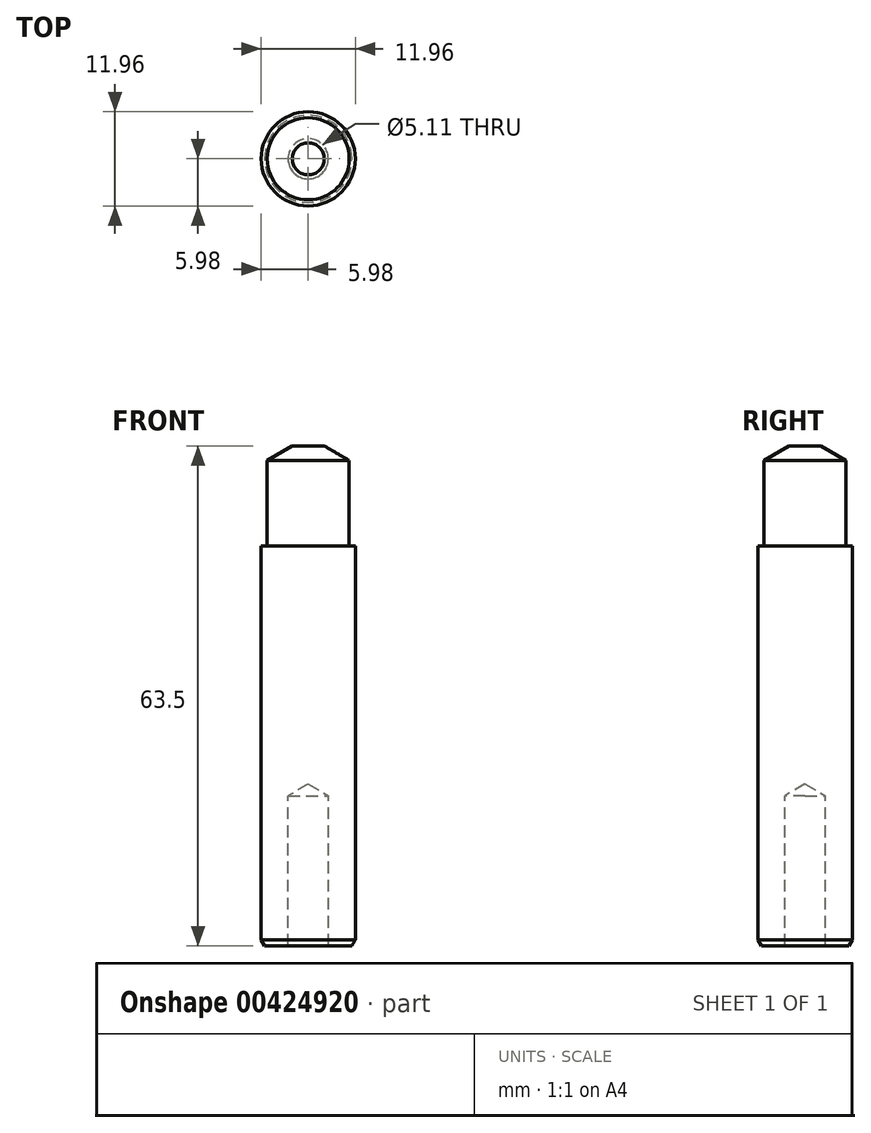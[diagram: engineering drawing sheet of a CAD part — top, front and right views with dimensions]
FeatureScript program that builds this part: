
annotation { "Feature Type Name" : "Feature", "Feature Type Description" : "" }
export const myFeature = defineFeature(function(context is Context, id is Id, definition is map)
    precondition{}
    {
        {
            var Q0;
            Q0=qCreatedBy(makeId("Top.planeOp"),FACE);
            var sketch = newSketch(context, id + "F0", { "sketchPlane" : qUnion([Q0])});
            skCircle(sketch, "E0", {"center": v(0, 0) * mm, "radius": 5.98 * mm});
            skSolve(sketch);
        }
        {
            var Q0;
            Q0=makeQuery(id+"F0.imprint","IMPRINT",FACE,{"disambiguationData":[TD([[makeQuery(id+"F0.imprint","IMPRINT",EDGE,{"derivedFrom":sQuery(id+"F0.wireOp",EDGE,"E0")}),1.0]])]});
            extrude(context, id + "F1", {"entities" : qUnion([Q0]), "depth" : 50.8 * mm, "symmetric" : true});
        }
        {
            var Q0;
            Q0=makeQuery(id+"F1.opExtrude","CAP_FACE",FACE,{"disambiguationData":[OSD([sQuery(id+"F0.wireOp",EDGE,"E0")])],"isStart":false});
            var sketch = newSketch(context, id + "F2", { "sketchPlane" : qUnion([Q0])});
            skCircle(sketch, "E1", {"center": v(0, 0) * mm, "radius": 5.2 * mm});
            skSolve(sketch);
        }
        {
            var Q0;
            Q0 = qSketchRegion(id + "F2", true);
            extrude(context, id + "F3", {"entities" : qUnion([Q0]), "operationType" : NewBodyOperationType.ADD, "depth" : 12.7 * mm});
        }
        {
            var Q0;
            Q0=makeQuery(id+"F3.opExtrude","CAP_EDGE",EDGE,{"disambiguationData":[OSD([sQuery(id+"F2.wireOp",EDGE,"E1")])],"isStart":false});
            chamfer(context, id + "F4", {"entities" : qUnion([Q0]), "chamferType" : ChamferType.OFFSET_ANGLE, "width" : 3.17 * mm, "oppositeDirection" : true, "angle" : 30 * degree, "tangentPropagation" : true});
        }
        {
            var Q0;
            Q0=makeQuery(id+"F1.opExtrude","CAP_EDGE",EDGE,{"disambiguationData":[OSD([sQuery(id+"F0.wireOp",EDGE,"E0")])],"isStart":true});
            chamfer(context, id + "F5", {"entities" : qUnion([Q0]), "chamferType" : ChamferType.OFFSET_ANGLE, "width" : 0.76 * mm, "oppositeDirection" : false, "angle" : 30 * degree, "tangentPropagation" : true});
        }
        {
            var Q0;
            Q0=makeQuery(id+"F1.opExtrude","CAP_FACE",FACE,{"disambiguationData":[OSD([sQuery(id+"F0.wireOp",EDGE,"E0")])],"isStart":true});
            var sketch = newSketch(context, id + "F6", { "sketchPlane" : qUnion([Q0])});
            skPoint(sketch, "E2", {"position": v(0, 0) * mm});
            skSolve(sketch);
        }
        {
            var Q0;
            Q0=sQuery(id+"F6.wireOp",VERTEX,"E2");
            var Q1;
            Q1=makeQuery(id+"F1.opExtrude","SWEPT_BODY",BODY,{"disambiguationData":[OSD([sQuery(id+"F0.wireOp",EDGE,"E0")])]});
            hole(context, id + "F7", {"style" : HoleStyle.SIMPLE, "endStyle" : HoleEndStyle.BLIND, "standardTappedOrClearance" : lookupTablePath({ "standard" : "ANSI", "engagement" : "75%", "pitch" : "20 tpi", "size" : "1/4", "type" : "Tapped" }), "standardBlindInLast" : lookupTablePath({ "standard" : "ANSI", "engagement" : "75%", "pitch" : "20 tpi", "size" : "1/4", "type" : "Tapped" }), "holeDiameter" : 5.1 * mm, "showTappedDepth" : true, "holeDepth" : 19.05 * mm, "isTappedThrough" : true, "tappedDepth" : 15.24 * mm, "tapClearance" : 3, "locations" : qUnion([Q0]), "scope" : qUnion([Q1]), "majorDiameter" : 6.35 * mm, "startStyle" : HoleStartStyle.SKETCH});
        }
    });
